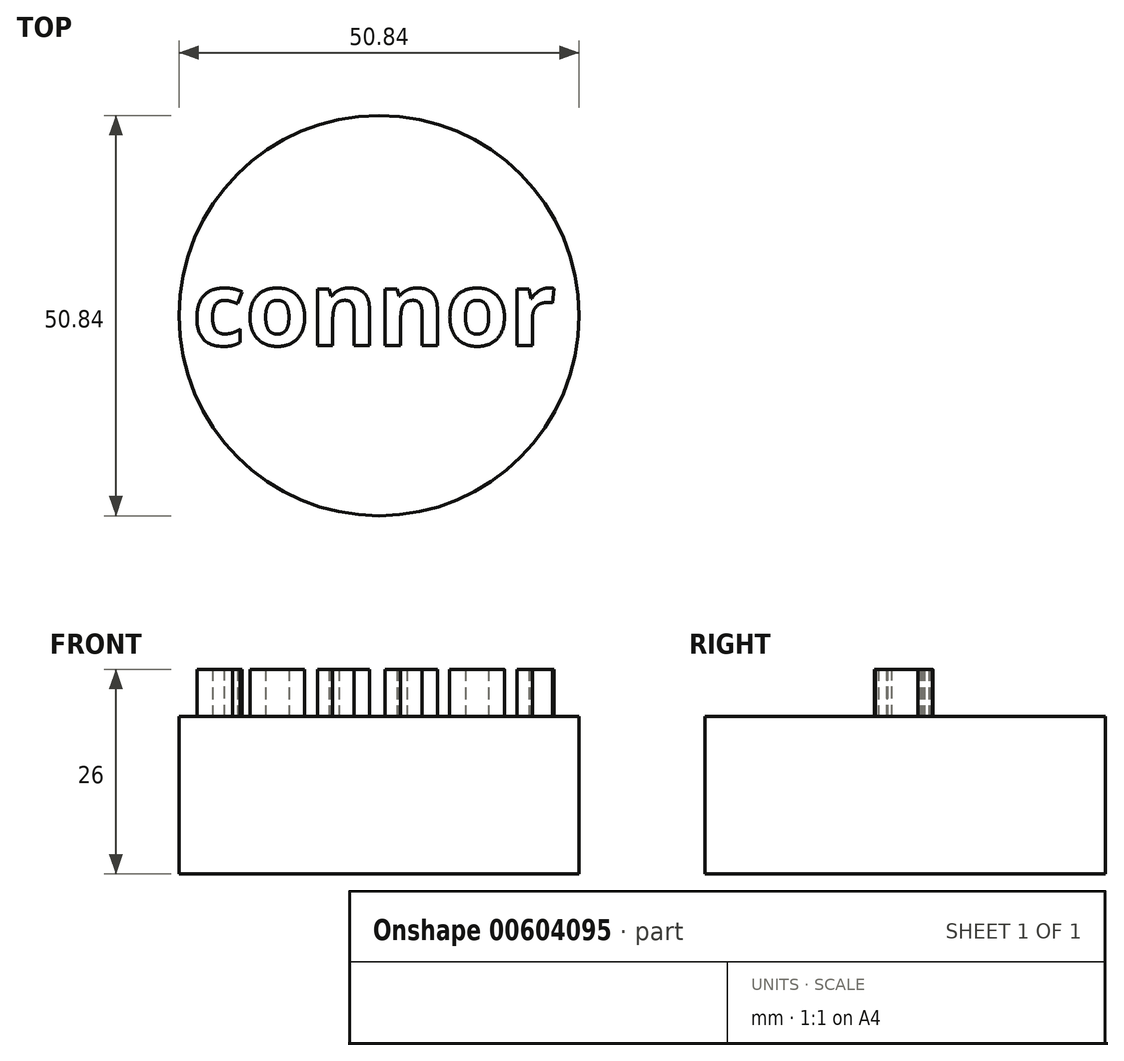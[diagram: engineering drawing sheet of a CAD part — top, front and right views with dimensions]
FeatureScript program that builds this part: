
annotation { "Feature Type Name" : "Feature", "Feature Type Description" : "" }
export const myFeature = defineFeature(function(context is Context, id is Id, definition is map)
    precondition{}
    {
        {
            var Q0;
            Q0=qCreatedBy(makeId("Top.planeOp"),FACE);
            var sketch = newSketch(context, id + "F0", { "sketchPlane" : qUnion([Q0])});
            skCircle(sketch, "E0", {"center": v(0, 0) * mm, "radius": 25.42 * mm});
            skSolve(sketch);
        }
        {
            var Q0;
            Q0=makeQuery(id+"F0.imprint","IMPRINT",FACE,{"disambiguationData":[TD([[makeQuery(id+"F0.imprint","IMPRINT",EDGE,{"derivedFrom":sQuery(id+"F0.wireOp",EDGE,"E0")}),1.0]])]});
            extrude(context, id + "F1", {"entities" : qUnion([Q0]), "depth" : 20 * mm, "offsetDistance" : 25 * mm});
        }
        {
            var Q0;
            Q0=makeQuery(id+"F1.opExtrude","CAP_FACE",FACE,{"disambiguationData":[OSD([sQuery(id+"F0.wireOp",EDGE,"E0")])],"isStart":false});
            var sketch = newSketch(context, id + "F2", { "sketchPlane" : qUnion([Q0])});
            skText(sketch, "E1", { "text": "connor", "fontName": "OpenSans-Bold.ttf"});
            const initialGuessF2  = {"E1": [-0.02373, -0.00378, 1, 0, 0.00945]};
            skSetInitialGuess(sketch, initialGuessF2);
            skSolve(sketch);
        }
        {
            var Q0;
            Q0 = qSketchRegion(id + "F2", true);
            extrude(context, id + "F3", {"entities" : qUnion([Q0]), "operationType" : NewBodyOperationType.ADD, "depth" : 6 * mm, "offsetDistance" : 25 * mm});
        }
    });
